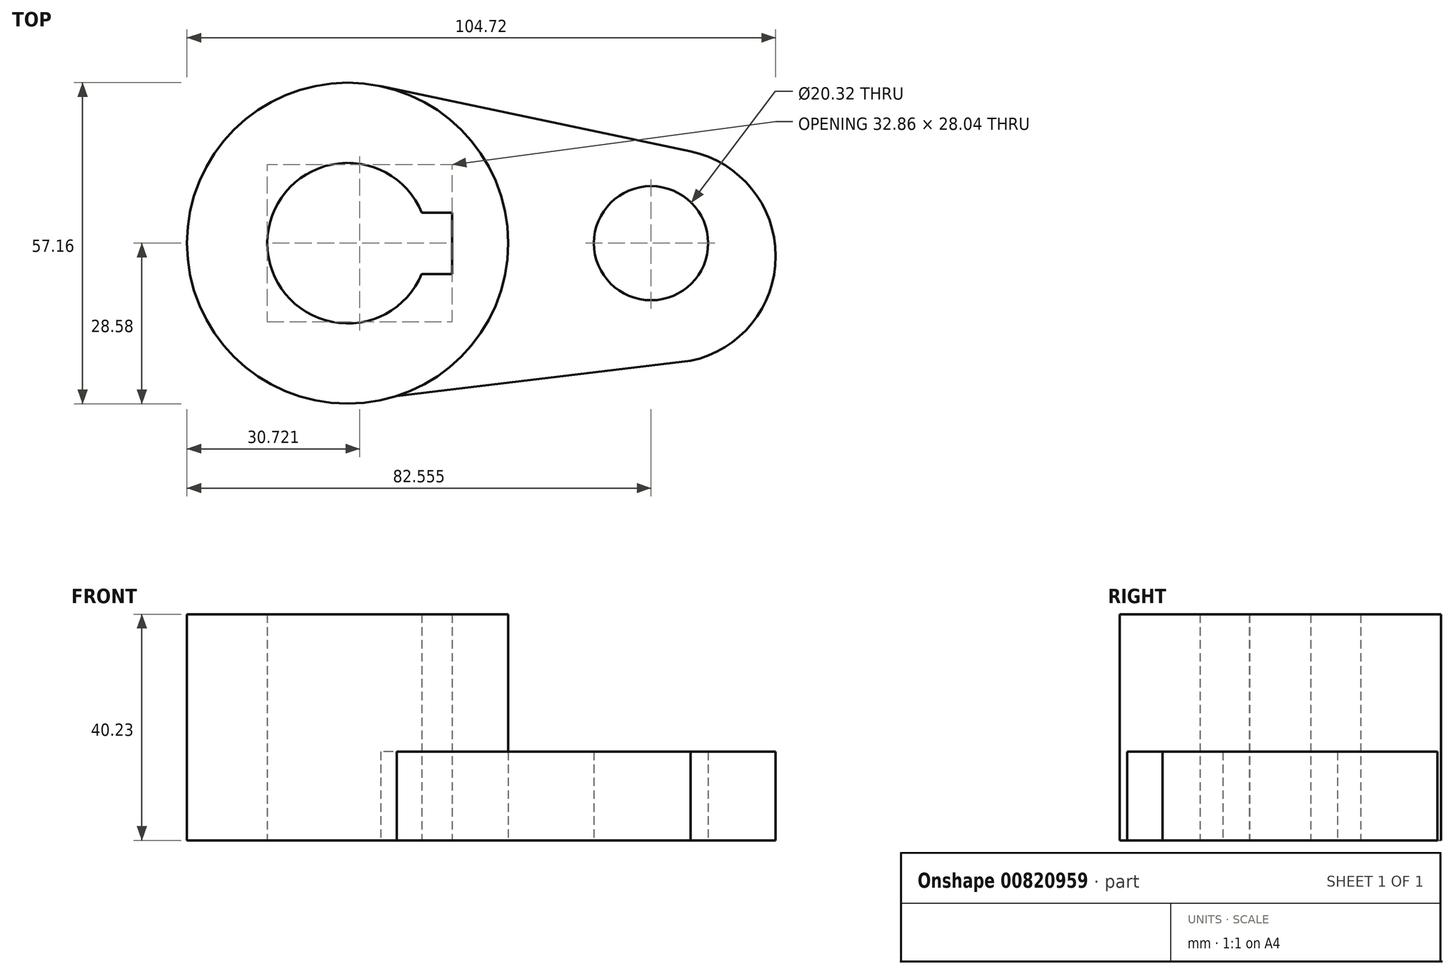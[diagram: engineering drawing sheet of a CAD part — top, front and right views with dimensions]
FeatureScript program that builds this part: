
annotation { "Feature Type Name" : "Feature", "Feature Type Description" : "" }
export const myFeature = defineFeature(function(context is Context, id is Id, definition is map)
    precondition{}
    {
        {
            var Q0;
            Q0=qCreatedBy(makeId("Top.planeOp"),FACE);
            var sketch = newSketch(context, id + "F0", { "sketchPlane" : qUnion([Q0])});
            skCircle(sketch, "E0", {"center": v(0, 0) * mm, "radius": 28.58 * mm});
            skCircle(sketch, "E1", {"center": v(0, 0) * mm, "radius": 25.64 * mm});
            skArc(sketch, "E2", {"start": v(13.22, 5.42) * mm, "mid": v(-14.29, 0) * mm, "end": v(13.22, -5.42) * mm});
            skLineSegment(sketch, "E3.bottom", {"start": v(13.22, 5.42) * mm, "end": v(18.57, 5.42) * mm});
            skLineSegment(sketch, "E3.top", {"start": v(13.22, -5.47) * mm, "end": v(18.57, -5.47) * mm});
            skLineSegment(sketch, "E3.left", {"start": v(13.22, -5.42) * mm, "end": v(13.22, -5.47) * mm});
            skLineSegment(sketch, "E3.right", {"start": v(18.57, 5.42) * mm, "end": v(18.57, -5.47) * mm});
            skCircle(sketch, "E4", {"center": v(53.98, 0) * mm, "radius": 10.16 * mm});
            skLineSegment(sketch, "E5", {"start": v(61.02, 16.33) * mm, "end": v(5.9, 27.96) * mm});
            skLineSegment(sketch, "E6", {"start": v(61.02, -20.95) * mm, "end": v(8.75, -27.2) * mm});
            skArc(sketch, "E7", {"start": v(61.02, -20.95) * mm, "mid": v(76.14, -2.3) * mm, "end": v(61.02, 16.33) * mm});
            skSolve(sketch);
        }
        {
            var Q0;
            Q0=makeQuery(id+"F0.imprint","IMPRINT",FACE,{"disambiguationData":[TD([[makeQuery(id+"F0.imprint","IMPRINT",EDGE,{"derivedFrom":sQuery(id+"F0.wireOp",EDGE,"E4")}),-1.0]])]});
            extrude(context, id + "F1", {"entities" : qUnion([Q0]), "depth" : 15.77 * mm, "offsetDistance" : 25.4 * mm});
        }
        {
            var Q0;
            Q0=makeQuery(id+"F0.imprint","IMPRINT",FACE,{"disambiguationData":[TD([[makeQuery(id+"F0.imprint","IMPRINT",EDGE,{"derivedFrom":sQuery(id+"F0.wireOp",EDGE,"E1")}),1.0]])]});
            var Q1;
            Q1=makeQuery(id+"F0.imprint","IMPRINT",FACE,{"disambiguationData":[TD([[makeQuery(id+"F0.imprint","IMPRINT",EDGE,{"derivedFrom":sQuery(id+"F0.wireOp",EDGE,"E1")}),-1.0]])]});
            extrude(context, id + "F2", {"entities" : qUnion([Q0, Q1]), "depth" : 40.23 * mm, "offsetDistance" : 25.4 * mm});
        }
    });
